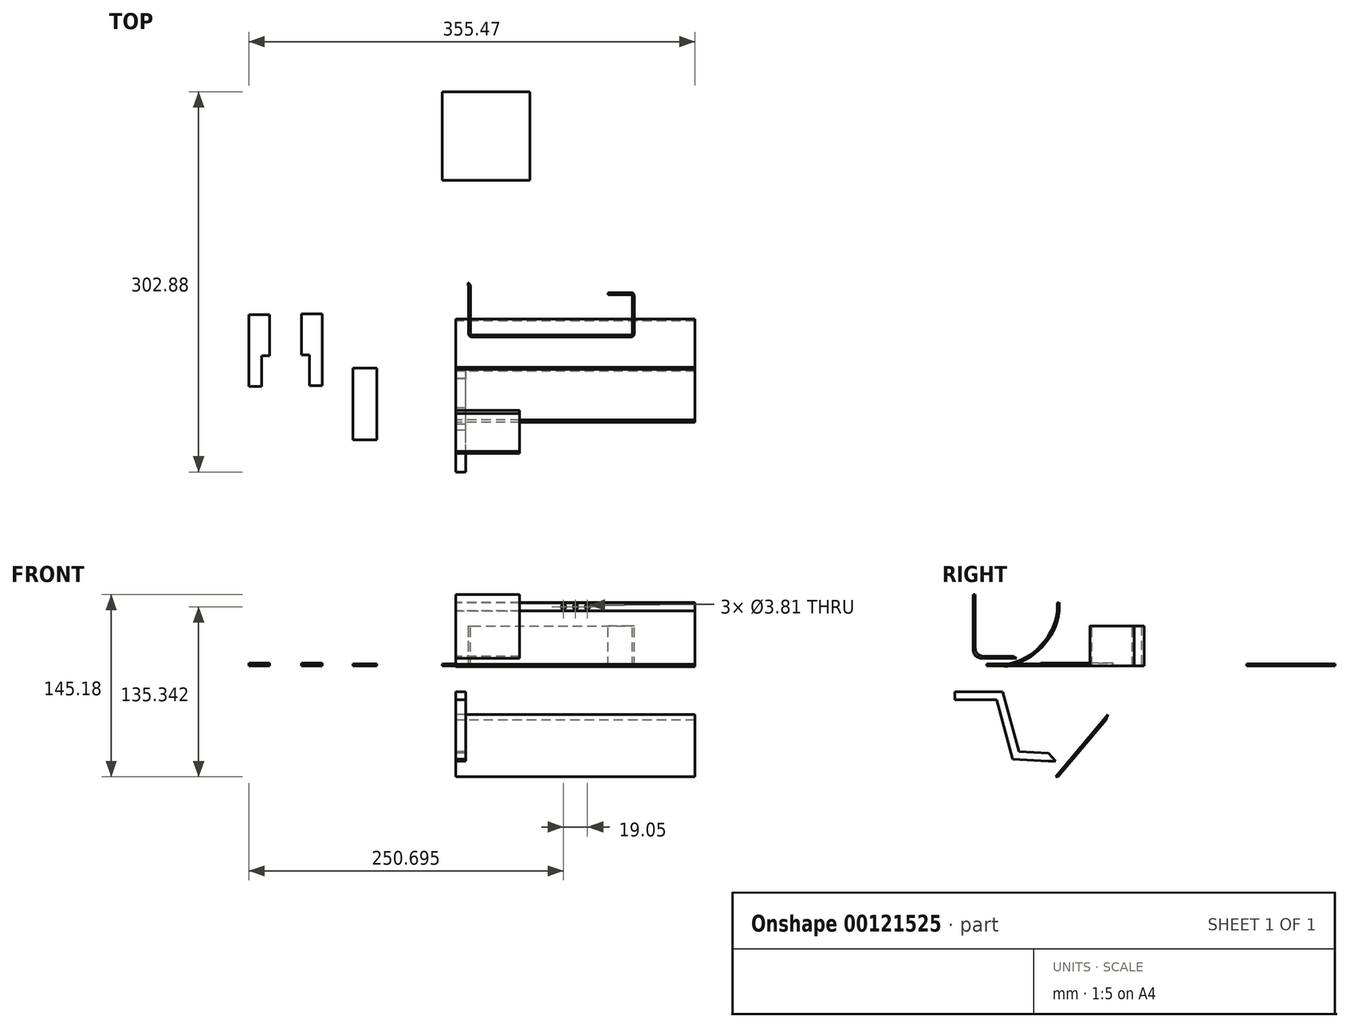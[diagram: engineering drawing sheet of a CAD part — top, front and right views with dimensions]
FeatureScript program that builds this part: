
annotation { "Feature Type Name" : "Feature", "Feature Type Description" : "" }
export const myFeature = defineFeature(function(context is Context, id is Id, definition is map)
    precondition{}
    {
        {
            var Q0;
            Q0=qCreatedBy(makeId("Right.planeOp"),FACE);
            var sketch = newSketch(context, id + "F0", { "sketchPlane" : qUnion([Q0])});
            skLineSegment(sketch, "E0", {"start": v(1.35, 50.25) * mm, "end": v(1.35, 43.9) * mm});
            skArc(sketch, "E1", {"start": v(-38.75, 1.42) * mm, "mid": v(-11.9, 16.23) * mm, "end": v(1.35, 43.9) * mm});
            skArc(sketch, "E2.0", {"start": v(-38.44, -0.15) * mm, "mid": v(-10.7, 15.17) * mm, "end": v(2.95, 43.79) * mm});
            skLineSegment(sketch, "E2.1", {"start": v(2.95, 50.58) * mm, "end": v(2.95, 43.79) * mm});
            skLineSegment(sketch, "E3", {"start": v(-38.44, -0.15) * mm, "end": v(-40.71, -0.6) * mm});
            skLineSegment(sketch, "E4", {"start": v(-40.71, -0.6) * mm, "end": v(-38.75, 1.42) * mm});
            skLineSegment(sketch, "E5", {"start": v(1.35, 50.25) * mm, "end": v(2.95, 50.58) * mm});
            skSolve(sketch);
        }
        {
            var Q0;
            Q0 = qSketchRegion(id + "F0", true);
            extrude(context, id + "F1", {"entities" : qUnion([Q0]), "depth" : 190.5 * mm});
        }
        {
            var Q0;
            Q0=qCreatedBy(makeId("Top.planeOp"),FACE);
            var sketch = newSketch(context, id + "F2", { "sketchPlane" : qUnion([Q0])});
            skLineSegment(sketch, "E6.bottom", {"start": v(-82.2, 2.34) * mm, "end": v(-63.14, 2.34) * mm});
            skLineSegment(sketch, "E6.top", {"start": v(-82.2, -54.81) * mm, "end": v(-63.14, -54.81) * mm});
            skLineSegment(sketch, "E6.left", {"start": v(-82.2, 2.34) * mm, "end": v(-82.2, -54.81) * mm});
            skLineSegment(sketch, "E6.right", {"start": v(-63.14, 2.34) * mm, "end": v(-63.14, -54.81) * mm});
            skSolve(sketch);
        }
        {
            var Q0;
            Q0 = qSketchRegion(id + "F2", true);
            extrude(context, id + "F3", {"entities" : qUnion([Q0]), "depth" : 1.6 * mm});
        }
        {
            var Q0;
            Q0=qCreatedBy(makeId("Right.planeOp"),FACE);
            var sketch = newSketch(context, id + "F4", { "sketchPlane" : qUnion([Q0])});
            skLineSegment(sketch, "E7", {"start": v(41.63, -38.54) * mm, "end": v(0, -88.16) * mm});
            skLineSegment(sketch, "E8.0", {"start": v(40.03, -42.94) * mm, "end": v(2.09, -88.16) * mm});
            skLineSegment(sketch, "E9", {"start": v(2.09, -88.16) * mm, "end": v(0, -88.16) * mm});
            skLineSegment(sketch, "E10", {"start": v(40.03, -42.94) * mm, "end": v(41.63, -38.54) * mm});
            skSolve(sketch);
        }
        {
            var Q0;
            Q0 = qSketchRegion(id + "F4", true);
            extrude(context, id + "F5", {"entities" : qUnion([Q0]), "depth" : 190.5 * mm});
        }
        {
            var Q0;
            Q0=qCreatedBy(makeId("Right.planeOp"),FACE);
            var sketch = newSketch(context, id + "F6", { "sketchPlane" : qUnion([Q0])});
            skLineSegment(sketch, "E11", {"start": v(-65.56, 57.02) * mm, "end": v(-65.56, 12.57) * mm});
            skLineSegment(sketch, "E12", {"start": v(-59.2, 6.22) * mm, "end": v(-33.8, 6.22) * mm});
            skPoint(sketch, "E13.visualSharp", {"position": v(-65.56, 6.22) * mm});
            skArc(sketch, "E13.filletArc", {"start": v(-65.56, 12.57) * mm, "mid": v(-63.7, 8.08) * mm, "end": v(-59.2, 6.22) * mm});
            skLineSegment(sketch, "E14.0", {"start": v(-57.6, 7.82) * mm, "end": v(-33.8, 7.82) * mm});
            skLineSegment(sketch, "E14.1", {"start": v(-63.96, 57.02) * mm, "end": v(-63.96, 14.17) * mm});
            skPoint(sketch, "E15.visualSharp", {"position": v(-63.96, 7.82) * mm});
            skArc(sketch, "E15.filletArc", {"start": v(-63.96, 14.17) * mm, "mid": v(-62.1, 9.68) * mm, "end": v(-57.6, 7.82) * mm});
            skLineSegment(sketch, "E16", {"start": v(-33.8, 7.82) * mm, "end": v(-31.2, 6.22) * mm});
            skLineSegment(sketch, "E17", {"start": v(-31.2, 6.22) * mm, "end": v(-33.8, 6.22) * mm});
            skLineSegment(sketch, "E18", {"start": v(-63.96, 57.02) * mm, "end": v(-65.56, 57.02) * mm});
            skSolve(sketch);
        }
        {
            var Q0;
            Q0 = qSketchRegion(id + "F6", true);
            extrude(context, id + "F7", {"entities" : qUnion([Q0]), "depth" : 50.8 * mm});
        }
        {
            var Q0;
            Q0=qCreatedBy(makeId("Top.planeOp"),FACE);
            var sketch = newSketch(context, id + "F8", { "sketchPlane" : qUnion([Q0])});
            skLineSegment(sketch, "E19.bottom", {"start": v(59.03, 152.1) * mm, "end": v(-10.9, 152.1) * mm});
            skLineSegment(sketch, "E19.top", {"start": v(59.03, 222.52) * mm, "end": v(-10.9, 222.52) * mm});
            skLineSegment(sketch, "E19.left", {"start": v(59.03, 152.1) * mm, "end": v(59.03, 222.52) * mm});
            skLineSegment(sketch, "E19.right", {"start": v(-10.9, 152.1) * mm, "end": v(-10.9, 222.52) * mm});
            skPoint(sketch, "E19.middle", {"position": v(24.06, 187.3) * mm});
            skSolve(sketch);
        }
        {
            var Q0;
            Q0 = qSketchRegion(id + "F8", true);
            var Q1;
            Q1=makeQuery(id+"F5.opExtrude","SWEPT_FACE",FACE,{"disambiguationData":[OSD([sQuery(id+"F4.wireOp",EDGE,"4177841b-ecdb-4ef6-896d-cbd4e28e22ba.0")])]});
            extrude(context, id + "F21", {"entities" : qUnion([Q0, Q1]), "depth" : 1.6 * mm});
        }
        {
            var Q0;
            Q0=qCreatedBy(makeId("Right.planeOp"),FACE);
            var sketch = newSketch(context, id + "F9", { "sketchPlane" : qUnion([Q0])});
            skLineSegment(sketch, "E20", {"start": v(-80.36, -20.34) * mm, "end": v(-42.26, -20.34) * mm});
            skLineSegment(sketch, "E21", {"start": v(-42.26, -20.34) * mm, "end": v(-29.19, -68.11) * mm});
            skLineSegment(sketch, "E22", {"start": v(-29.19, -68.11) * mm, "end": v(-5.76, -69.47) * mm});
            skLineSegment(sketch, "E23.0", {"start": v(-34.1, -74.19) * mm, "end": v(-6.13, -75.81) * mm});
            skLineSegment(sketch, "E23.1", {"start": v(-47.1, -26.69) * mm, "end": v(-34.1, -74.19) * mm});
            skLineSegment(sketch, "E23.2", {"start": v(-80.36, -26.69) * mm, "end": v(-47.1, -26.69) * mm});
            skLineSegment(sketch, "E24", {"start": v(-80.36, -20.34) * mm, "end": v(-80.36, -26.69) * mm});
            skLineSegment(sketch, "E25", {"start": v(-5.76, -69.47) * mm, "end": v(0, -75.81) * mm});
            skLineSegment(sketch, "E26", {"start": v(0, -75.81) * mm, "end": v(0, -75.81) * mm});
            skLineSegment(sketch, "E27", {"start": v(0, -75.81) * mm, "end": v(-6.13, -75.81) * mm});
            skSolve(sketch);
        }
        {
            var Q0;
            Q0 = qSketchRegion(id + "F9", true);
            extrude(context, id + "F22", {"entities" : qUnion([Q0]), "depth" : 7.94 * mm});
        }
        {
            var Q0;
            Q0=makeQuery(id+"F1.opExtrude","SWEPT_FACE",FACE,{"disambiguationData":[OSD([sQuery(id+"F0.wireOp",EDGE,"E2.1")])]});
            var sketch = newSketch(context, id + "F10", { "sketchPlane" : qUnion([Q0])});
            skCircle(sketch, "E28", {"center": v(-95.25, 47.18) * mm, "radius": 1.9 * mm});
            skPoint(sketch, "E28.centerSnap0", {"position": v(-190.5, 47.18) * mm});
            skPoint(sketch, "E28.centerSnap1", {"position": v(-95.25, 43.79) * mm});
            skCircle(sketch, "E29.1.0.0", {"center": v(-85.73, 47.18) * mm, "radius": 1.9 * mm});
            skLineSegment(sketch, "E29.direction1", {"start": v(-95.25, 47.18) * mm, "end": v(-85.73, 47.18) * mm, "construction": true});
            skCircle(sketch, "E30.1.0.0", {"center": v(-104.78, 47.18) * mm, "radius": 1.9 * mm});
            skLineSegment(sketch, "E30.direction1", {"start": v(-95.25, 47.18) * mm, "end": v(-104.78, 47.18) * mm, "construction": true});
            skSolve(sketch);
        }
        {
            var Q0;
            Q0 = qSketchRegion(id + "F10", true);
            extrude(context, id + "F11", {"entities" : qUnion([Q0]), "operationType" : NewBodyOperationType.REMOVE, "endBound" : BoundingType.THROUGH_ALL, "oppositeDirection" : true, "depth" : 25.4 * mm});
        }
        {
            var Q0;
            Q0=qCreatedBy(makeId("Top.planeOp"),FACE);
            var sketch = newSketch(context, id + "F12", { "sketchPlane" : qUnion([Q0])});
            skLineSegment(sketch, "E31", {"start": v(-164.97, -12.13) * mm, "end": v(-164.97, 45.02) * mm});
            skLineSegment(sketch, "E32", {"start": v(-164.97, 45.02) * mm, "end": v(-148.46, 45.02) * mm});
            skLineSegment(sketch, "E33", {"start": v(-148.46, 45.02) * mm, "end": v(-148.46, 12.15) * mm});
            skLineSegment(sketch, "E34", {"start": v(-148.46, 12.15) * mm, "end": v(-154.81, 12.15) * mm});
            skLineSegment(sketch, "E35", {"start": v(-154.81, 12.15) * mm, "end": v(-154.81, -12.13) * mm});
            skLineSegment(sketch, "E36", {"start": v(-154.81, -12.13) * mm, "end": v(-164.97, -12.13) * mm});
            skSolve(sketch);
        }
        {
            var Q0;
            Q0 = qSketchRegion(id + "F12", true);
            extrude(context, id + "F13", {"entities" : qUnion([Q0]), "depth" : 2.3 * mm});
        }
        {
            var Q0;
            Q0=qCreatedBy(makeId("Top.planeOp"),FACE);
            var sketch = newSketch(context, id + "F14", { "sketchPlane" : qUnion([Q0])});
            skLineSegment(sketch, "E37", {"start": v(-106.4, 45.65) * mm, "end": v(-106.4, -11.5) * mm});
            skLineSegment(sketch, "E38", {"start": v(-106.4, 45.65) * mm, "end": v(-122.9, 45.65) * mm});
            skLineSegment(sketch, "E39", {"start": v(-122.9, 45.65) * mm, "end": v(-122.9, 12.79) * mm});
            skLineSegment(sketch, "E40", {"start": v(-122.9, 12.79) * mm, "end": v(-116.55, 12.79) * mm});
            skLineSegment(sketch, "E41", {"start": v(-116.55, 12.79) * mm, "end": v(-116.55, -11.5) * mm});
            skLineSegment(sketch, "E42", {"start": v(-116.55, -11.5) * mm, "end": v(-106.4, -11.5) * mm});
            skSolve(sketch);
        }
        {
            var Q0;
            Q0 = qSketchRegion(id + "F14", true);
            extrude(context, id + "F15", {"entities" : qUnion([Q0]), "depth" : 2.3 * mm});
        }
        {
            var Q0;
            Q0=qCreatedBy(makeId("Right.planeOp"),FACE);
            var sketch = newSketch(context, id + "F16", { "sketchPlane" : qUnion([Q0])});
            skLineSegment(sketch, "E43.bottom", {"start": v(69.18, 0) * mm, "end": v(70.78, 0) * mm});
            skLineSegment(sketch, "E43.top", {"start": v(69.18, 31.75) * mm, "end": v(70.78, 31.75) * mm});
            skLineSegment(sketch, "E43.left", {"start": v(69.18, 0) * mm, "end": v(69.18, 31.75) * mm});
            skLineSegment(sketch, "E43.right", {"start": v(70.78, 0) * mm, "end": v(70.78, 31.75) * mm});
            skSolve(sketch);
        }
        {
            var Q0;
            Q0=qCreatedBy(makeId("Top.planeOp"),FACE);
            var sketch = newSketch(context, id + "F17", { "sketchPlane" : qUnion([Q0])});
            skLineSegment(sketch, "E44", {"start": v(0, 69.31) * mm, "end": v(7.96, 69.31) * mm});
            skLineSegment(sketch, "E45", {"start": v(10.24, 67.03) * mm, "end": v(10.24, 29.69) * mm});
            skLineSegment(sketch, "E46", {"start": v(12.53, 27.4) * mm, "end": v(139.53, 27.4) * mm});
            skLineSegment(sketch, "E47", {"start": v(141.82, 29.69) * mm, "end": v(141.82, 60.17) * mm});
            skLineSegment(sketch, "E48", {"start": v(139.53, 62.46) * mm, "end": v(121.2, 62.46) * mm});
            skPoint(sketch, "E49.visualSharp", {"position": v(10.24, 27.4) * mm});
            skArc(sketch, "E49.filletArc", {"start": v(10.24, 29.69) * mm, "mid": v(10.91, 28.07) * mm, "end": v(12.53, 27.4) * mm});
            skPoint(sketch, "E50.visualSharp", {"position": v(10.24, 69.31) * mm});
            skArc(sketch, "E50.filletArc", {"start": v(10.24, 67.03) * mm, "mid": v(9.57, 68.64) * mm, "end": v(7.96, 69.31) * mm});
            skPoint(sketch, "E51.visualSharp", {"position": v(141.82, 27.4) * mm});
            skArc(sketch, "E51.filletArc", {"start": v(139.53, 27.4) * mm, "mid": v(141.15, 28.07) * mm, "end": v(141.82, 29.69) * mm});
            skPoint(sketch, "E52.visualSharp", {"position": v(141.82, 62.46) * mm});
            skArc(sketch, "E52.filletArc", {"start": v(141.82, 60.17) * mm, "mid": v(141.15, 61.79) * mm, "end": v(139.53, 62.46) * mm});
            skSolve(sketch);
        }
        {
            var Q0;
            Q0=makeQuery(id+"F16.imprint","IMPRINT",FACE,{"disambiguationData":[TD([[makeQuery(id+"F16.imprint","IMPRINT",EDGE,{"derivedFrom":sQuery(id+"F16.wireOp",EDGE,"E43.bottom")}),1.0]])]});
            var Q1;
            Q1 = qConstructionFilter(qBodyType(qCreatedBy(id + "F17" ,EDGE), BodyType.WIRE), ConstructionObject.NO);
            sweep(context, id + "F18", {"profiles" : qUnion([Q0]), "path" : qUnion([Q1])});
        }
        {
            var Q0;
            Q0=makeQuery(id+"F18.opSweep","SWEPT_FACE",FACE,{"disambiguationData":[OSD([sQuery(id+"F16.wireOp",EDGE,"E43.right"),sQuery(id+"F17.wireOp",EDGE,"E44")])]});
            var sketch = newSketch(context, id + "F19", { "sketchPlane" : qUnion([Q0])});
            skLineSegment(sketch, "E53", {"start": v(0, 0) * mm, "end": v(-9.63, 0) * mm});
            skLineSegment(sketch, "E54", {"start": v(-9.63, 0) * mm, "end": v(-9.63, 31.75) * mm});
            skLineSegment(sketch, "E55", {"start": v(-9.63, 31.75) * mm, "end": v(0, 31.75) * mm});
            skLineSegment(sketch, "E56", {"start": v(0, 31.75) * mm, "end": v(0, 0) * mm});
            skSolve(sketch);
        }
        {
            var Q0;
            Q0 = qSketchRegion(id + "F19", true);
            extrude(context, id + "F20", {"entities" : qUnion([Q0]), "operationType" : NewBodyOperationType.REMOVE, "oppositeDirection" : true, "depth" : 25.4 * mm});
        }
    });
